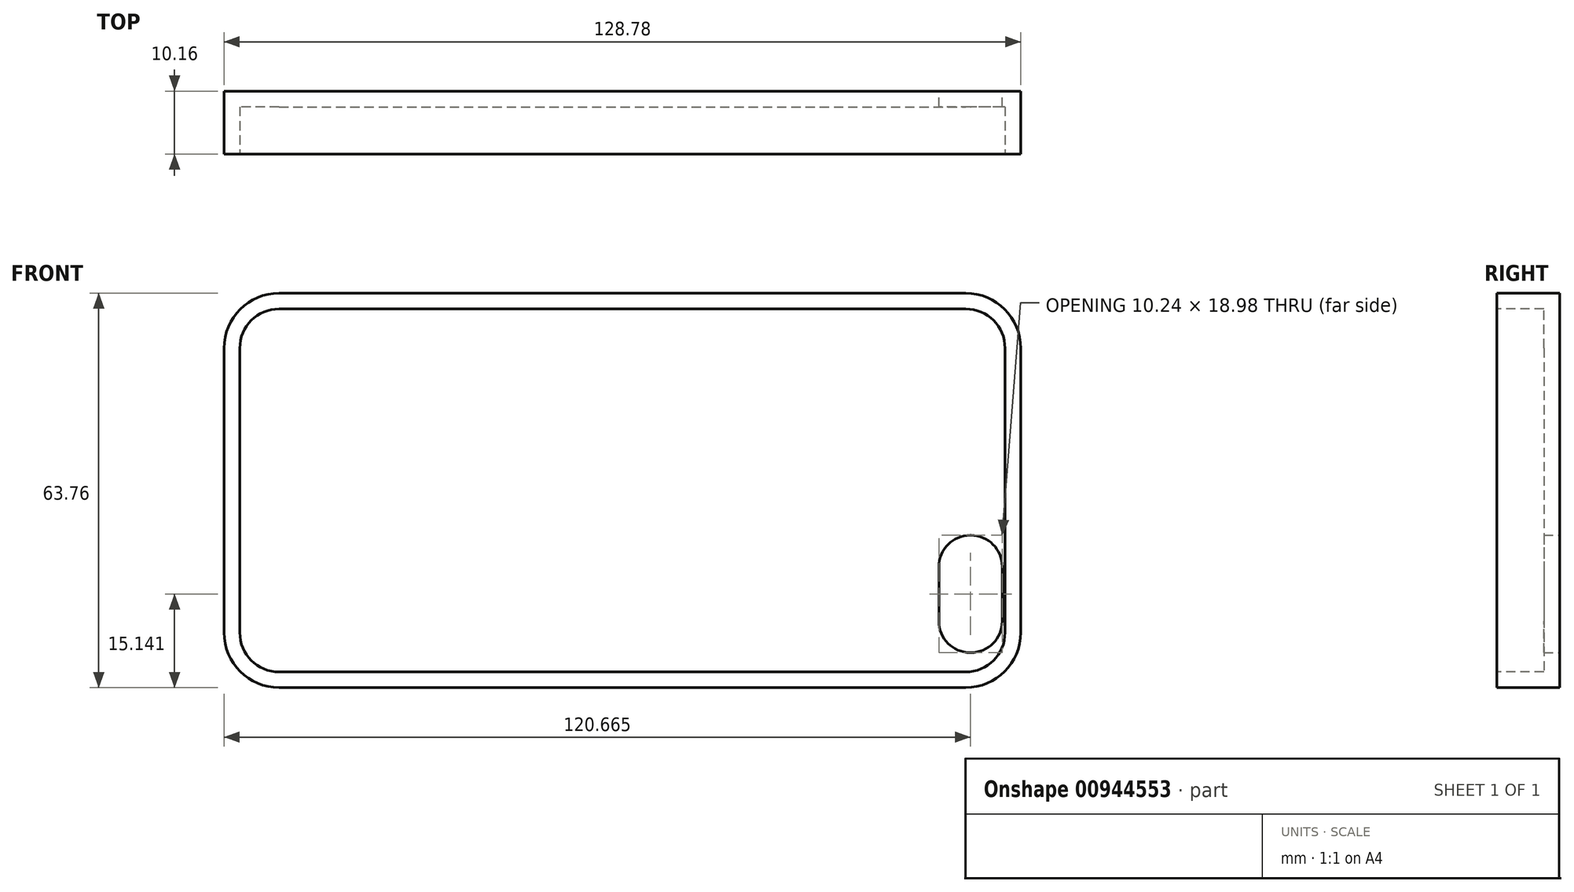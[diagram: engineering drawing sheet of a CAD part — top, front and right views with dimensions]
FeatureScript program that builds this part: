
annotation { "Feature Type Name" : "Feature", "Feature Type Description" : "" }
export const myFeature = defineFeature(function(context is Context, id is Id, definition is map)
    precondition{}
    {
        {
            var Q0;
            Q0=qCreatedBy(makeId("Front.planeOp"),FACE);
            var sketch = newSketch(context, id + "F0", { "sketchPlane" : qUnion([Q0])});
            skLineSegment(sketch, "E0.bottom", {"start": v(-55.5, 31.88) * mm, "end": v(55.5, 31.88) * mm});
            skLineSegment(sketch, "E0.top", {"start": v(-55.5, -31.88) * mm, "end": v(55.5, -31.88) * mm});
            skLineSegment(sketch, "E0.left", {"start": v(-64.39, 22.99) * mm, "end": v(-64.39, -22.99) * mm});
            skLineSegment(sketch, "E0.right", {"start": v(64.39, 22.99) * mm, "end": v(64.39, -22.99) * mm});
            skPoint(sketch, "E0.middle", {"position": v(0, 0) * mm});
            skPoint(sketch, "E1.visualSharp", {"position": v(-64.39, 31.88) * mm});
            skArc(sketch, "E1.filletArc", {"start": v(-55.5, 31.88) * mm, "mid": v(-61.79, 29.27) * mm, "end": v(-64.39, 22.99) * mm});
            skPoint(sketch, "E2.visualSharp", {"position": v(64.39, 31.88) * mm});
            skArc(sketch, "E2.filletArc", {"start": v(64.39, 22.99) * mm, "mid": v(61.79, 29.27) * mm, "end": v(55.5, 31.88) * mm});
            skPoint(sketch, "E3.visualSharp", {"position": v(64.39, -31.88) * mm});
            skArc(sketch, "E3.filletArc", {"start": v(55.5, -31.88) * mm, "mid": v(61.79, -29.27) * mm, "end": v(64.39, -22.99) * mm});
            skPoint(sketch, "E4.visualSharp", {"position": v(-64.39, -31.88) * mm});
            skArc(sketch, "E4.filletArc", {"start": v(-64.39, -22.99) * mm, "mid": v(-61.79, -29.27) * mm, "end": v(-55.5, -31.88) * mm});
            skSolve(sketch);
        }
        {
            var Q0;
            Q0=makeQuery(id+"F0.imprint","IMPRINT",FACE,{"disambiguationData":[TD([[makeQuery(id+"F0.imprint","IMPRINT",EDGE,{"derivedFrom":sQuery(id+"F0.wireOp",EDGE,"E0.bottom")}),-1.0]])]});
            extrude(context, id + "F1", {"entities" : qUnion([Q0]), "depth" : 10.16 * mm, "offsetDistance" : 25.4 * mm});
        }
        {
            var Q0;
            Q0=makeQuery(id+"F1.opExtrude","CAP_FACE",FACE,{"disambiguationData":[OSD([sQuery(id+"F0.wireOp",EDGE,"E0.bottom"),sQuery(id+"F0.wireOp",EDGE,"E0.top"),sQuery(id+"F0.wireOp",EDGE,"E0.left"),sQuery(id+"F0.wireOp",EDGE,"E0.right"),sQuery(id+"F0.wireOp",EDGE,"E1.filletArc"),sQuery(id+"F0.wireOp",EDGE,"E2.filletArc"),sQuery(id+"F0.wireOp",EDGE,"E3.filletArc"),sQuery(id+"F0.wireOp",EDGE,"E4.filletArc")])],"isStart":false});
            var sketch = newSketch(context, id + "F2", { "sketchPlane" : qUnion([Q0])});
            skLineSegment(sketch, "E5.bottom", {"start": v(-55.5, 29.34) * mm, "end": v(55.5, 29.34) * mm});
            skLineSegment(sketch, "E5.top", {"start": v(-55.5, -29.34) * mm, "end": v(55.5, -29.34) * mm});
            skLineSegment(sketch, "E5.left", {"start": v(-61.85, 22.99) * mm, "end": v(-61.85, -22.99) * mm});
            skLineSegment(sketch, "E5.right", {"start": v(61.85, 22.99) * mm, "end": v(61.85, -22.99) * mm});
            skPoint(sketch, "E5.middle", {"position": v(0, 0) * mm});
            skPoint(sketch, "E6.visualSharp", {"position": v(-61.85, 29.34) * mm});
            skArc(sketch, "E6.filletArc", {"start": v(-55.5, 29.34) * mm, "mid": v(-59.99, 27.48) * mm, "end": v(-61.85, 22.99) * mm});
            skPoint(sketch, "E7.visualSharp", {"position": v(61.85, 29.34) * mm});
            skArc(sketch, "E7.filletArc", {"start": v(61.85, 22.99) * mm, "mid": v(59.99, 27.48) * mm, "end": v(55.5, 29.34) * mm});
            skPoint(sketch, "E8.visualSharp", {"position": v(61.85, -29.34) * mm});
            skArc(sketch, "E8.filletArc", {"start": v(55.5, -29.34) * mm, "mid": v(59.99, -27.48) * mm, "end": v(61.85, -22.99) * mm});
            skPoint(sketch, "E9.visualSharp", {"position": v(-61.85, -29.34) * mm});
            skArc(sketch, "E9.filletArc", {"start": v(-61.85, -22.99) * mm, "mid": v(-59.99, -27.48) * mm, "end": v(-55.5, -29.34) * mm});
            skSolve(sketch);
        }
        {
            var Q0;
            Q0=makeQuery(id+"F2.imprint","IMPRINT",FACE,{"disambiguationData":[TD([[makeQuery(id+"F2.imprint","IMPRINT",EDGE,{"derivedFrom":sQuery(id+"F2.wireOp",EDGE,"E5.bottom")}),-1.0]])]});
            extrude(context, id + "F3", {"entities" : qUnion([Q0]), "operationType" : NewBodyOperationType.REMOVE, "oppositeDirection" : true, "depth" : 7.62 * mm, "offsetDistance" : 25.4 * mm});
        }
        {
            var Q0;
            Q0=makeQuery(id+"F1.opExtrude","CAP_FACE",FACE,{"disambiguationData":[OSD([sQuery(id+"F0.wireOp",EDGE,"E0.bottom"),sQuery(id+"F0.wireOp",EDGE,"E0.top"),sQuery(id+"F0.wireOp",EDGE,"E0.left"),sQuery(id+"F0.wireOp",EDGE,"E0.right"),sQuery(id+"F0.wireOp",EDGE,"E1.filletArc"),sQuery(id+"F0.wireOp",EDGE,"E2.filletArc"),sQuery(id+"F0.wireOp",EDGE,"E3.filletArc"),sQuery(id+"F0.wireOp",EDGE,"E4.filletArc")])],"isStart":true});
            var sketch = newSketch(context, id + "F4", { "sketchPlane" : qUnion([Q0])});
            skLineSegment(sketch, "E10.bottom", {"start": v(-56.31, -26.23) * mm, "end": v(-56.24, -26.23) * mm});
            skLineSegment(sketch, "E10.top", {"start": v(-56.31, -7.25) * mm, "end": v(-56.24, -7.25) * mm});
            skLineSegment(sketch, "E10.left", {"start": v(-61.4, -21.15) * mm, "end": v(-61.4, -12.33) * mm});
            skLineSegment(sketch, "E10.right", {"start": v(-51.16, -21.15) * mm, "end": v(-51.16, -12.33) * mm});
            skPoint(sketch, "E11.visualSharp", {"position": v(-61.4, -7.25) * mm});
            skArc(sketch, "E11.filletArc", {"start": v(-56.31, -7.25) * mm, "mid": v(-59.9, -8.74) * mm, "end": v(-61.4, -12.33) * mm});
            skPoint(sketch, "E12.visualSharp", {"position": v(-51.16, -26.23) * mm});
            skArc(sketch, "E12.filletArc", {"start": v(-56.24, -26.23) * mm, "mid": v(-52.64, -24.74) * mm, "end": v(-51.16, -21.15) * mm});
            skPoint(sketch, "E13.visualSharp", {"position": v(-51.16, -7.25) * mm});
            skArc(sketch, "E13.filletArc", {"start": v(-51.16, -12.33) * mm, "mid": v(-52.64, -8.74) * mm, "end": v(-56.24, -7.25) * mm});
            skPoint(sketch, "E14.visualSharp", {"position": v(-61.4, -26.23) * mm});
            skArc(sketch, "E14.filletArc", {"start": v(-61.4, -21.15) * mm, "mid": v(-59.9, -24.74) * mm, "end": v(-56.31, -26.23) * mm});
            skSolve(sketch);
        }
        {
            var Q0;
            Q0=qSketchRegion(id+"F4",true);
            extrude(context, id + "F5", {"entities" : qUnion([Q0]), "operationType" : NewBodyOperationType.REMOVE, "oppositeDirection" : true, "depth" : 25.4 * mm, "offsetDistance" : 25.4 * mm});
        }
    });
